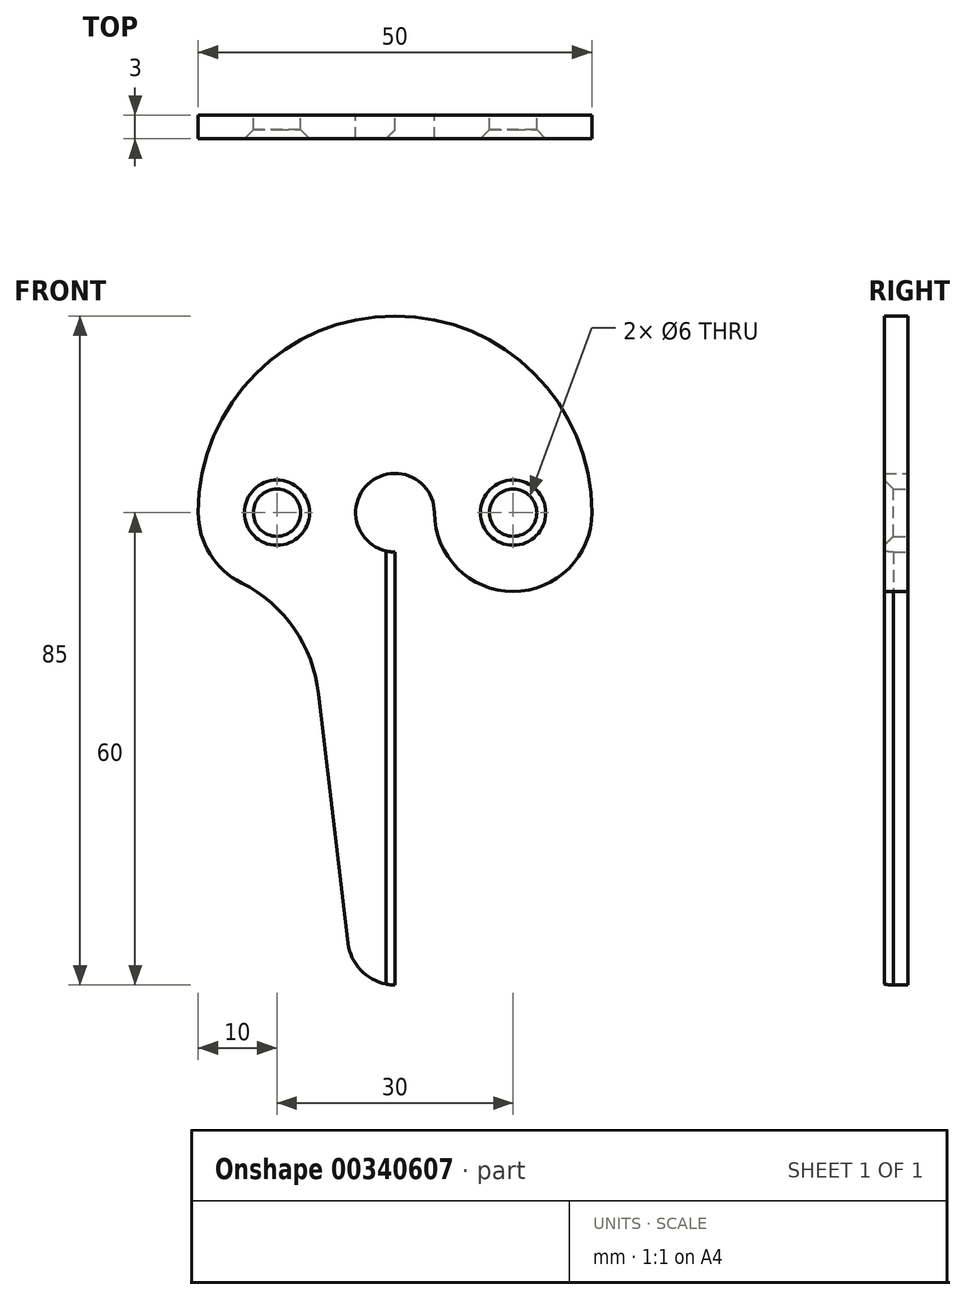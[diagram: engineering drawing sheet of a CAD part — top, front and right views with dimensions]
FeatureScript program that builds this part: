
annotation { "Feature Type Name" : "Feature", "Feature Type Description" : "" }
export const myFeature = defineFeature(function(context is Context, id is Id, definition is map)
    precondition{}
    {
        {
            var Q0;
            Q0=qCreatedBy(makeId("Front.planeOp"),FACE);
            var sketch = newSketch(context, id + "F0", { "sketchPlane" : qUnion([Q0])});
            skPoint(sketch, "E0", {"position": v(-15, 0) * mm});
            skPoint(sketch, "E1", {"position": v(15, 0) * mm});
            skArc(sketch, "E2", {"start": v(-25, 0) * mm, "mid": v(-23.52, -5.24) * mm, "end": v(-19.5, -8.93) * mm});
            skPoint(sketch, "E3", {"position": v(-27.6, -25) * mm});
            skArc(sketch, "E4", {"start": v(25, 0) * mm, "mid": v(0, 25) * mm, "end": v(-25, 0) * mm});
            skArc(sketch, "E5", {"start": v(5, 0) * mm, "mid": v(15, -10) * mm, "end": v(25, 0) * mm});
            skArc(sketch, "E6", {"start": v(5, 0) * mm, "mid": v(-3.54, 3.54) * mm, "end": v(0, -5) * mm});
            skArc(sketch, "E7", {"start": v(-9.72, -23.03) * mm, "mid": v(-12.82, -14.74) * mm, "end": v(-19.5, -8.93) * mm});
            skLineSegment(sketch, "E8", {"start": v(-3, -5) * mm, "end": v(-3, -4) * mm});
            skLineSegment(sketch, "E9", {"start": v(-3, -4) * mm, "end": v(-3, -59.2) * mm});
            skArc(sketch, "E10", {"start": v(-5.96, -54.7) * mm, "mid": v(-3.98, -58.49) * mm, "end": v(0, -60) * mm});
            skLineSegment(sketch, "E11", {"start": v(-9.72, -23.03) * mm, "end": v(-5.96, -54.7) * mm});
            skCircle(sketch, "E12", {"center": v(-15, 0) * mm, "radius": 3 * mm});
            skCircle(sketch, "E13", {"center": v(-15, 0) * mm, "radius": 3.5 * mm});
            skCircle(sketch, "E14", {"center": v(15, 0) * mm, "radius": 3 * mm});
            skCircle(sketch, "E15", {"center": v(15, 0) * mm, "radius": 3.5 * mm});
            skLineSegment(sketch, "E16", {"start": v(0, -5) * mm, "end": v(0, -60) * mm});
            skSolve(sketch);
        }
        {
            var Q0;
            Q0=makeQuery(id+"F0.imprint","IMPRINT",FACE,{"disambiguationData":[TD([[makeQuery(id+"F0.imprint","IMPRINT",EDGE,{"derivedFrom":sQuery(id+"F0.wireOp",EDGE,"E2")}),1.0]])]});
            var Q1;
            {var subQ6=sQuery(id+"F0.wireOp",EDGE,"E16");Q1=makeQuery(id+"F0.imprint","IMPRINT",FACE,{"disambiguationData":[TD([[makeQuery(id+"F0.imprint","IMPRINT",EDGE,{"derivedFrom":subQ6}),-1.0]])]});}
            var Q2;
            Q2=makeQuery(id+"F0.imprint","IMPRINT",FACE,{"disambiguationData":[TD([[makeQuery(id+"F0.imprint","IMPRINT",EDGE,{"derivedFrom":sQuery(id+"F0.wireOp",EDGE,"E14")}),-1.0]])]});
            var Q3;
            Q3=makeQuery(id+"F0.imprint","IMPRINT",FACE,{"disambiguationData":[TD([[makeQuery(id+"F0.imprint","IMPRINT",EDGE,{"derivedFrom":sQuery(id+"F0.wireOp",EDGE,"E12")}),-1.0]])]});
            extrude(context, id + "F1", {"entities" : qUnion([Q0, Q1, Q2, Q3]), "depth" : 3 * mm});
        }
        {
            var Q0;
            Q0=makeQuery(id+"F1.opExtrude","CAP_EDGE",EDGE,{"disambiguationData":[OSD([sQuery(id+"F0.wireOp",EDGE,"E16")])],"isStart":false});
            var Q1;
            Q1=makeQuery(id+"F1.opExtrude","CAP_EDGE",EDGE,{"disambiguationData":[OSD([sQuery(id+"F0.wireOp",EDGE,"E14")])],"isStart":false});
            var Q2;
            Q2=makeQuery(id+"F1.opExtrude","CAP_EDGE",EDGE,{"disambiguationData":[OSD([sQuery(id+"F0.wireOp",EDGE,"E12")])],"isStart":false});
            chamfer(context, id + "F2", {"entities" : qUnion([Q0, Q1, Q2]), "width" : 1.14 * mm, "tangentPropagation" : true});
        }
    });
